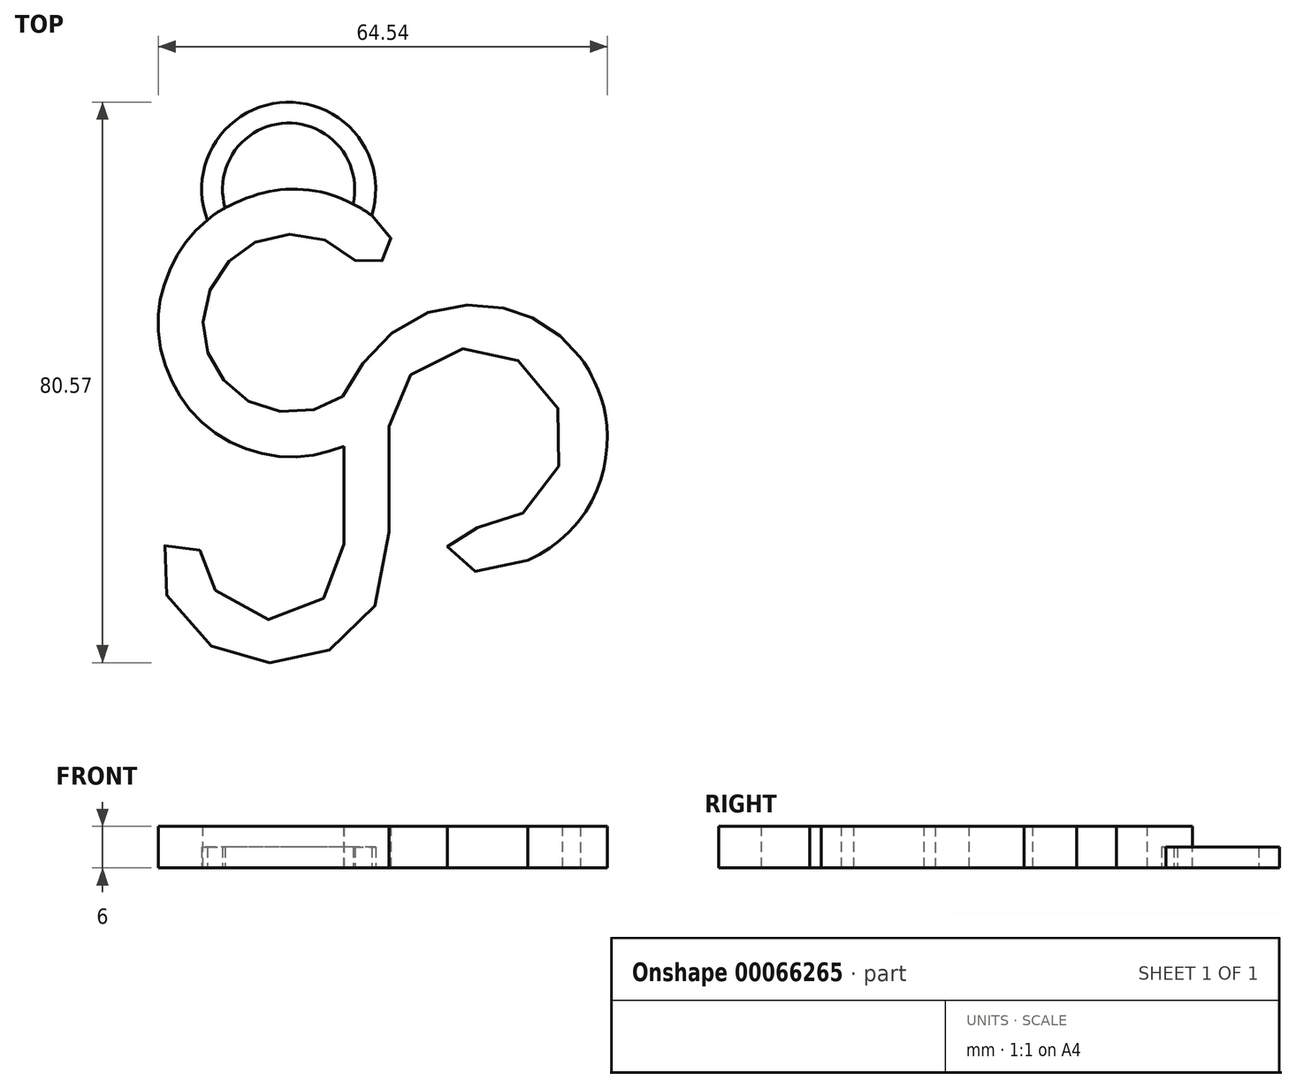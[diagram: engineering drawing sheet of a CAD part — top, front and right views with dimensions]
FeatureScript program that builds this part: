
annotation { "Feature Type Name" : "Feature", "Feature Type Description" : "" }
export const myFeature = defineFeature(function(context is Context, id is Id, definition is map)
    precondition{}
    {
        {
            var Q0;
            Q0=qCreatedBy(makeId("Top.planeOp"),FACE);
            var sketch = newSketch(context, id + "F0", { "sketchPlane" : qUnion([Q0])});
            skFitSpline(sketch, "E0", {"points": [v(-61.71, -18.93) * mm, v(-65.76, -20.17) * mm, v(-70.78, -20.44) * mm, v(-75.64, -19.34) * mm, v(-79.98, -17.16) * mm, v(-83.8, -13.74) * mm, v(-86.3, -9.79) * mm, v(-88.01, -4.91) * mm, v(-88.35, 0) * mm, v(-87.73, 3.63) * mm, v(-86.05, 7.81) * mm, v(-83.65, 11.31) * mm, v(-80.78, 14.03) * mm, v(-77.84, 15.8) * mm, v(-73.5, 17.43) * mm, v(-69.63, 18.02) * mm, v(-65.3, 17.67) * mm, v(-61.42, 16.38) * mm, v(-57.9, 14.38) * mm, v(-56.2, 12.82) * mm, v(-55.13, 11.65) * mm, v(-54.9, 10.47) * mm, v(-55.08, 9.07) * mm, v(-55.72, 8.07) * mm, v(-56.72, 7.48) * mm, v(-58.3, 7.07) * mm, v(-59.89, 7.6) * mm, v(-61.64, 9.07) * mm, v(-63.87, 10.47) * mm, v(-66.4, 11.3) * mm, v(-68.62, 11.53) * mm, v(-71.44, 11.35) * mm, v(-73.67, 10.7) * mm, v(-75.43, 9.83) * mm, v(-77.13, 8.6) * mm, v(-78.6, 7.25) * mm, v(-80, 5.43) * mm, v(-81, 3.44) * mm, v(-81.7, 1.38) * mm, v(-81.94, -0.67) * mm, v(-81.82, -2.72) * mm, v(-81.59, -4.3) * mm, v(-80.92, -6.3) * mm, v(-80.04, -7.93) * mm, v(-78.93, -9.48) * mm, v(-77.64, -10.88) * mm, v(-76, -12.1) * mm, v(-74.05, -13.1) * mm, v(-72.1, -13.73) * mm, v(-69.8, -14.02) * mm, v(-67.7, -13.99) * mm, v(-65.52, -13.54) * mm, v(-63.37, -12.7) * mm, v(-62.08, -11.92) * mm, v(-60.86, -10.3) * mm, v(-59.18, -7.35) * mm, v(-56.85, -4.4) * mm, v(-54.67, -2.55) * mm, v(-51.89, -0.73) * mm, v(-48.74, 0.56) * mm, v(-45.67, 1.22) * mm, v(-42.89, 1.39) * mm, v(-40.15, 1.18) * mm, v(-38.15, 0.81) * mm, v(-36.77, 0.38) * mm, v(-35, -0.34) * mm, v(-32.98, -1.36) * mm, v(-31.37, -2.48) * mm, v(-29.73, -3.9) * mm, v(-28.54, -5.11) * mm, v(-27.73, -6.16) * mm], "startDerivative": vector(-215.5, -78.71) * mm, "endDerivative": vector(70.79, -104) * mm});
            skFitSpline(sketch, "E1", {"points": [v(-27.73, -6.16) * mm, v(-27.25, -6.8) * mm, v(-26.47, -8.04) * mm, v(-26.1, -8.78) * mm, v(-25.62, -9.75) * mm, v(-25.04, -11.14) * mm, v(-24.52, -12.71) * mm, v(-24.13, -14.46) * mm, v(-23.88, -16.42) * mm, v(-23.88, -18.7) * mm, v(-24.19, -21.29) * mm, v(-24.85, -23.88) * mm, v(-25.86, -26.38) * mm, v(-27.45, -29.05) * mm, v(-29.87, -31.75) * mm, v(-32.36, -33.71) * mm, v(-35.3, -35.31) * mm], "startDerivative": vector(11.35, -14.61) * mm, "endDerivative": vector(-38.56, -18.37) * mm});
            skFitSpline(sketch, "E2", {"points": [v(-35.3, -35.31) * mm, v(-36.8, -35.85) * mm, v(-38.06, -36.24) * mm, v(-40.11, -36.65) * mm, v(-42.4, -36.9) * mm, v(-44.26, -36.9) * mm, v(-45.7, -36.21) * mm, v(-46.27, -35.64) * mm, v(-46.68, -34.8) * mm, v(-46.84, -33.82) * mm, v(-46.72, -32.73) * mm, v(-46.19, -31.77) * mm, v(-45.52, -31.1) * mm, v(-44.82, -30.69) * mm, v(-43.79, -30.6) * mm, v(-42.49, -30.6) * mm, v(-40.9, -30.54) * mm, v(-39.87, -30.38) * mm, v(-38.24, -29.82) * mm, v(-36.95, -29.12) * mm, v(-35.41, -28.13) * mm, v(-33.23, -26.02) * mm, v(-31.9, -24.18) * mm, v(-31.16, -22.63) * mm, v(-30.48, -20.58) * mm, v(-30.24, -18.49) * mm, v(-30.3, -16.33) * mm, v(-30.75, -13.98) * mm, v(-31.83, -11.57) * mm, v(-33.24, -9.48) * mm, v(-34.89, -7.8) * mm, v(-37.2, -6.33) * mm, v(-39.26, -5.52) * mm, v(-41.16, -5.03) * mm, v(-42.98, -4.88) * mm, v(-45.45, -5.05) * mm, v(-47.74, -5.85) * mm, v(-49.5, -6.7) * mm, v(-51.34, -7.95) * mm, v(-53.05, -9.75) * mm, v(-54.2, -11.44) * mm, v(-54.91, -13.09) * mm, v(-55.2, -14.9) * mm, v(-55.26, -19.94) * mm, v(-55.21, -28.02) * mm, v(-55.26, -34.01) * mm, v(-55.53, -36.84) * mm, v(-56.59, -40.5) * mm, v(-58.1, -43.25) * mm, v(-59.75, -45.19) * mm, v(-61.47, -46.75) * mm, v(-64.04, -48.32) * mm, v(-66.52, -49.28) * mm, v(-68.53, -49.76) * mm, v(-70.82, -50) * mm, v(-73.66, -50) * mm, v(-76.07, -49.56) * mm, v(-78.24, -48.88) * mm, v(-80.3, -47.92) * mm, v(-82.3, -46.59) * mm, v(-84.5, -44.5) * mm, v(-86.47, -41.78) * mm, v(-87.73, -38.94) * mm, v(-88.17, -37.47) * mm, v(-88.36, -35.31) * mm, v(-88.06, -34.02) * mm, v(-87.19, -33.04) * mm, v(-86.05, -32.5) * mm, v(-85.18, -32.4) * mm, v(-84.2, -32.47) * mm, v(-83.44, -32.88) * mm, v(-82.64, -33.53) * mm, v(-82.15, -34.44) * mm, v(-81.92, -35.31) * mm, v(-81.85, -36.25) * mm, v(-81.55, -37.31) * mm, v(-80.92, -38.49) * mm, v(-79.65, -40.3) * mm, v(-78.1, -41.67) * mm, v(-75.83, -43.1) * mm, v(-73.22, -43.79) * mm, v(-70.34, -43.79) * mm, v(-67.73, -43.07) * mm, v(-65.95, -42) * mm, v(-64.5, -40.65) * mm, v(-63.3, -39.16) * mm, v(-62.28, -37.09) * mm, v(-61.78, -35.31) * mm, v(-61.68, -31.68) * mm, v(-61.68, -25.71) * mm, v(-61.71, -18.93) * mm], "startDerivative": vector(-161.2, -58.6) * mm, "endDerivative": vector(-2.68, 341.43) * mm});
            skLineSegment(sketch, "E3", {"start": v(-88.36, -35.31) * mm, "end": v(-88.36, 22.16) * mm, "construction": true});
            skLineSegment(sketch, "E4", {"start": v(-23.88, -16.42) * mm, "end": v(-23.88, -44.1) * mm, "construction": true});
            skFitSpline(sketch, "E5.0", {"points": [v(-68.5, 31.77) * mm, v(-69.63, 31.89) * mm, v(-70.76, 31.77) * mm, v(-71.82, 31.44) * mm, v(-72.76, 30.94) * mm, v(-73.6, 30.32) * mm, v(-74.34, 29.6) * mm, v(-75.2, 28.52) * mm, v(-76.07, 27.02) * mm, v(-76.74, 25.33) * mm, v(-77.16, 23.88) * mm, v(-77.5, 22.38) * mm, v(-77.73, 20.82) * mm, v(-77.84, 19.23) * mm, v(-77.87, 18.02) * mm, v(-77.84, 16.8) * mm, v(-77.73, 15.22) * mm, v(-77.5, 13.66) * mm, v(-77.16, 12.16) * mm, v(-76.74, 10.7) * mm, v(-76.07, 9.02) * mm, v(-75.2, 7.52) * mm, v(-74.34, 6.44) * mm, v(-73.6, 5.72) * mm, v(-72.76, 5.1) * mm, v(-71.82, 4.6) * mm, v(-70.76, 4.27) * mm, v(-69.63, 4.15) * mm, v(-68.5, 4.27) * mm, v(-67.45, 4.6) * mm, v(-66.5, 5.1) * mm, v(-65.66, 5.72) * mm, v(-64.93, 6.44) * mm, v(-64.07, 7.52) * mm, v(-63.2, 9.02) * mm, v(-62.53, 10.7) * mm, v(-62.1, 12.16) * mm, v(-61.77, 13.66) * mm, v(-61.54, 15.22) * mm, v(-61.43, 16.8) * mm, v(-61.4, 18.02) * mm, v(-61.43, 19.23) * mm, v(-61.54, 20.82) * mm, v(-61.77, 22.38) * mm, v(-62.1, 23.88) * mm, v(-62.53, 25.33) * mm, v(-63.2, 27.02) * mm, v(-64.07, 28.52) * mm, v(-64.93, 29.6) * mm, v(-65.66, 30.32) * mm, v(-66.5, 30.94) * mm, v(-67.45, 31.44) * mm, v(-68.5, 31.77) * mm, v(-69.63, 31.89) * mm, v(-70.76, 31.77) * mm, v(-68.5, 31.77) * mm]});
            skArc(sketch, "E6", {"start": v(-60.38, 15.88) * mm, "mid": v(-69.91, 27.51) * mm, "end": v(-78.75, 15.33) * mm});
            skArc(sketch, "E7.0", {"start": v(-57.72, 14.24) * mm, "mid": v(-69.97, 30.51) * mm, "end": v(-81.32, 13.6) * mm});
            skSolve(sketch);
        }
        {
            var Q0;
            {var subQ11=sQuery(id+"F0.wireOp",EDGE,"E1");Q0=makeQuery(id+"F0.imprint","IMPRINT",FACE,{"disambiguationData":[TD([[makeQuery(id+"F0.imprint","IMPRINT",EDGE,{"derivedFrom":subQ11}),-1.0]])]});}
            extrude(context, id + "F1", {"entities" : qUnion([Q0]), "depth" : 6 * mm});
        }
        {
            var Q0;
            {var subQ0=sQuery(id+"F0.wireOp",EDGE,"E6");Q0=makeQuery(id+"F0.imprint","IMPRINT",FACE,{"disambiguationData":[TD([[makeQuery(id+"F0.imprint","IMPRINT",EDGE,{"derivedFrom":subQ0}),-1.0]])]});}
            extrude(context, id + "F2", {"entities" : qUnion([Q0]), "operationType" : NewBodyOperationType.ADD, "depth" : 3 * mm});
        }
    });
